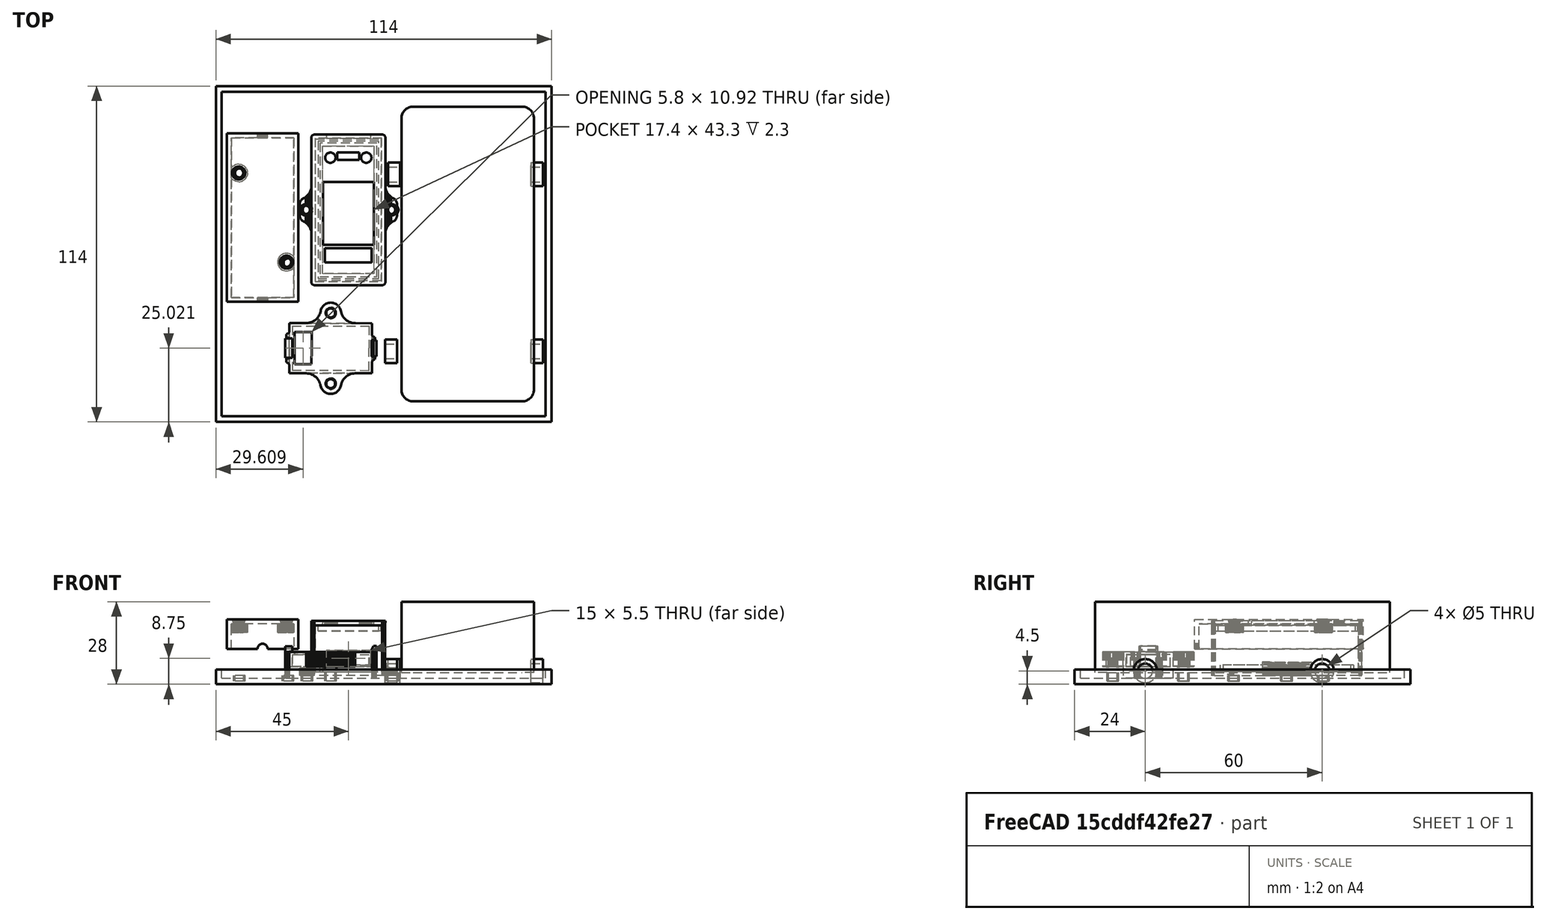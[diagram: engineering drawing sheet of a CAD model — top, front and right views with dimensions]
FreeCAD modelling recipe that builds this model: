
FCSTD DOCUMENT  (FreeCAD 0.18R16131 (Git))
Label: ardulexa-caja-v2
License: All rights reserved
LicenseURL: http://en.wikipedia.org/wiki/All_rights_reserved
objects: Part::Cylinder×20, Part::Cut×11, Part::Feature×6, Part::Box×3, Part::MultiFuse×1, Part::Fillet×1
note: 42 computed .brp shape members not serialized (recipe doc carries the construction recipe); baked Part::Feature solids carry a one-line shape summary decoded from their .brp

FEATURE [Part::Feature] buck_box_bottom_plate001001_solid  label="buck_box_bottom_plate002 (Solid)"
  Placement = pos=(-27,35,-22) rot=(0,0,1;4.71239rad)
  shape: bbox 24.25 x 57.25 x 10 mm, 504 faces (baked)
FEATURE [Part::Feature] __relay_Lid001001_solid  label="__relay_Lid002 (Solid)"
  Placement = pos=(4e-16,0,-4) rot=(0,1,0;3.14159rad)
  shape: bbox 25.1 x 51.1 x 3.5 mm, 222 faces (baked)
FEATURE [Part::Feature] buck_box_top_plate001001_solid  label="buck_box_top_plate002 (Solid)"
  Placement = pos=(-27,35,-22) rot=(0,0,1;4.71239rad)
  shape: bbox 24.25 x 57.25 x 14.1 mm, 287 faces (baked)
FEATURE [Part::Feature] __relay_Case001001_solid  label="__relay_Case002 (Solid)"
  Placement = pos=(5e-16,0,-4) rot=(0,1,0;3.14159rad)
  shape: bbox 33 x 51 x 17 mm, 1131 faces (baked)
FEATURE [Part::Feature] ESP8266_Bottom_Case001_solid001  label="ESP8266_Bottom_Case001 (Solid)001"
  shape: bbox 30.02 x 30.98 x 5 mm, 311 faces (baked)
FEATURE [Part::Feature] ESP8266_Top_Lid001_solid001  label="ESP8266_Top_Lid001 (Solid)001"
  shape: bbox 31 x 17 x 11 mm, 115 faces (baked)
FEATURE [Part::MultiFuse] Fusion  label="ESP8266"
  Placement = pos=(8,-38,-16) rot=(-1,0,0;3.14159rad)
  Shapes = -> [ESP8266_Top_Lid001_solid001,ESP8266_Bottom_Case001_solid001]
FEATURE [Part::Box] Box  label="CubeInner"
  AttacherType = Attacher::AttachEngine3D
  Height = 5
  Length = 110
  Placement = pos=(-29,-61,-22) rot=(0,0,1;0rad)
  Width = 110
FEATURE [Part::Box] Box001  label="Cube001"
  AttacherType = Attacher::AttachEngine3D
  Height = 24
  Length = 45
  Placement = pos=(32,-56,-20) rot=(0,0,1;0rad)
  Width = 100
FEATURE [Part::Fillet] Fillet  label="Enchufe_referencia"
  Base = -> Box001
  Edges = 4 edges r=4: [Edge1,Edge3,Edge5,Edge7]
FEATURE [Part::Box] Box002  label="CubeOuter"
  AttacherType = Attacher::AttachEngine3D
  Height = 5
  Length = 114
  Placement = pos=(-31,-63,-24) rot=(0,0,1;0rad)
  Width = 114
FEATURE [Part::Cut] Cut  label="Case"
  Base = -> Box002
  Tool = -> Box
FEATURE [Part::Cylinder] Cylinder  label="CylinderOuter"
  Angle = 360
  AttacherType = Attacher::AttachEngine3D
  Height = 5
  Placement = pos=(8,-26,-23) rot=(0,0,1;0rad)
  Radius = 1.5
FEATURE [Part::Cylinder] Cylinder001  label="CylinderInner"
  Angle = 360
  AttacherType = Attacher::AttachEngine3D
  Height = 5
  Placement = pos=(8,-26,-23) rot=(0,0,1;0rad)
  Radius = 2
FEATURE [Part::Cut] Cut001  label="espsup001"
  Base = -> Cylinder001
  Tool = -> Cylinder
FEATURE [Part::Cylinder] Cylinder002  label="CylinderInner001"
  Angle = 360
  AttacherType = Attacher::AttachEngine3D
  Height = 5
  Placement = pos=(8,-26,-23) rot=(0,0,1;0rad)
  Radius = 2
FEATURE [Part::Cylinder] Cylinder003  label="CylinderOuter001"
  Angle = 360
  AttacherType = Attacher::AttachEngine3D
  Height = 5
  Placement = pos=(8,-26,-23) rot=(0,0,1;0rad)
  Radius = 1.5
FEATURE [Part::Cut] Cut002  label="espsup002"
  Base = -> Cylinder002
  Placement = pos=(0,-24,0) rot=(0,0,1;0rad)
  Tool = -> Cylinder003
FEATURE [Part::Cylinder] Cylinder004  label="CylinderInner002"
  Angle = 360
  AttacherType = Attacher::AttachEngine3D
  Height = 4
  Placement = pos=(8,-26,-23) rot=(0,0,1;0rad)
  Radius = 2
FEATURE [Part::Cylinder] Cylinder005  label="CylinderOuter002"
  Angle = 360
  AttacherType = Attacher::AttachEngine3D
  Height = 4
  Placement = pos=(8,-26,-23) rot=(0,0,1;0rad)
  Radius = 1.5
FEATURE [Part::Cut] Cut003  label="relaysupp01"
  Base = -> Cylinder004
  Placement = pos=(-8,35,0) rot=(0,0,1;0rad)
  Tool = -> Cylinder005
FEATURE [Part::Cylinder] Cylinder006  label="CylinderInner003"
  Angle = 360
  AttacherType = Attacher::AttachEngine3D
  Height = 4
  Placement = pos=(8,-26,-23) rot=(0,0,1;0rad)
  Radius = 2
FEATURE [Part::Cylinder] Cylinder007  label="CylinderOuter003"
  Angle = 360
  AttacherType = Attacher::AttachEngine3D
  Height = 4
  Placement = pos=(8,-26,-23) rot=(0,0,1;0rad)
  Radius = 1.5
FEATURE [Part::Cut] Cut004  label="relaysupp002"
  Base = -> Cylinder006
  Placement = pos=(21,35,0) rot=(0,0,1;0rad)
  Tool = -> Cylinder007
FEATURE [Part::Cylinder] Cylinder008  label="CylinderInner004"
  Angle = 360
  AttacherType = Attacher::AttachEngine3D
  Height = 2
  Placement = pos=(8,-26,-23) rot=(0,0,1;0rad)
  Radius = 2
FEATURE [Part::Cylinder] Cylinder009  label="CylinderOuter004"
  Angle = 360
  AttacherType = Attacher::AttachEngine3D
  Height = 2
  Placement = pos=(8,-26,-23) rot=(0,0,1;0rad)
  Radius = 1.5
FEATURE [Part::Cut] Cut005  label="bucksupp001"
  Base = -> Cylinder008
  Placement = pos=(-31,47.5,0) rot=(0,0,1;0rad)
  Tool = -> Cylinder009
FEATURE [Part::Cylinder] Cylinder010  label="CylinderOuter005"
  Angle = 360
  AttacherType = Attacher::AttachEngine3D
  Height = 2
  Placement = pos=(8,-26,-23) rot=(0,0,1;0rad)
  Radius = 1.5
FEATURE [Part::Cylinder] Cylinder011  label="CylinderInner005"
  Angle = 360
  AttacherType = Attacher::AttachEngine3D
  Height = 2
  Placement = pos=(8,-26,-23) rot=(0,0,1;0rad)
  Radius = 2
FEATURE [Part::Cut] Cut006  label="bucksupp002"
  Base = -> Cylinder011
  Placement = pos=(-14.5,17,0) rot=(0,0,1;0rad)
  Tool = -> Cylinder010
FEATURE [Part::Cylinder] Cylinder012  label="Cylinder"
  Angle = 360
  AttacherType = Attacher::AttachEngine3D
  Height = 10
  Placement = pos=(23.5,-39,-22) rot=(0,1,0;1.5708rad)
  Radius = 2.5
FEATURE [Part::Cylinder] Cylinder013  label="Cylinder001"
  Angle = 360
  AttacherType = Attacher::AttachEngine3D
  Height = 4
  Placement = pos=(26.5,-39,-22) rot=(0,1,0;1.5708rad)
  Radius = 4
FEATURE [Part::Cut] Cut007  label="bricksup001"
  Base = -> Cylinder013
  Placement = pos=(0,0,2.5) rot=(0,0,1;0rad)
  Tool = -> Cylinder012
FEATURE [Part::Cylinder] Cylinder014  label="Cylinder002"
  Angle = 360
  AttacherType = Attacher::AttachEngine3D
  Height = 10
  Placement = pos=(23.5,-39,-22) rot=(0,1,0;1.5708rad)
  Radius = 2.5
FEATURE [Part::Cylinder] Cylinder015  label="Cylinder003"
  Angle = 360
  AttacherType = Attacher::AttachEngine3D
  Height = 4
  Placement = pos=(26.5,-39,-22) rot=(0,1,0;1.5708rad)
  Radius = 4
FEATURE [Part::Cut] Cut008  label="bricksup002"
  Base = -> Cylinder015
  Placement = pos=(1,60,2.5) rot=(0,0,1;0rad)
  Tool = -> Cylinder014
FEATURE [Part::Cylinder] Cylinder016  label="Cylinder004"
  Angle = 360
  AttacherType = Attacher::AttachEngine3D
  Height = 10
  Placement = pos=(23.5,-39,-22) rot=(0,1,0;1.5708rad)
  Radius = 2.5
FEATURE [Part::Cylinder] Cylinder017  label="Cylinder005"
  Angle = 360
  AttacherType = Attacher::AttachEngine3D
  Height = 4
  Placement = pos=(26.5,-39,-22) rot=(0,1,0;1.5708rad)
  Radius = 4
FEATURE [Part::Cut] Cut009  label="bricksup003"
  Base = -> Cylinder017
  Placement = pos=(49.5,60,2.5) rot=(0,0,1;0rad)
  Tool = -> Cylinder016
FEATURE [Part::Cylinder] Cylinder018  label="Cylinder006"
  Angle = 360
  AttacherType = Attacher::AttachEngine3D
  Height = 10
  Placement = pos=(23.5,-39,-22) rot=(0,1,0;1.5708rad)
  Radius = 2.5
FEATURE [Part::Cylinder] Cylinder019  label="Cylinder007"
  Angle = 360
  AttacherType = Attacher::AttachEngine3D
  Height = 4
  Placement = pos=(26.5,-39,-22) rot=(0,1,0;1.5708rad)
  Radius = 4
FEATURE [Part::Cut] Cut010  label="bricksup004"
  Base = -> Cylinder019
  Placement = pos=(49.5,0,2.5) rot=(0,0,1;0rad)
  Tool = -> Cylinder018
